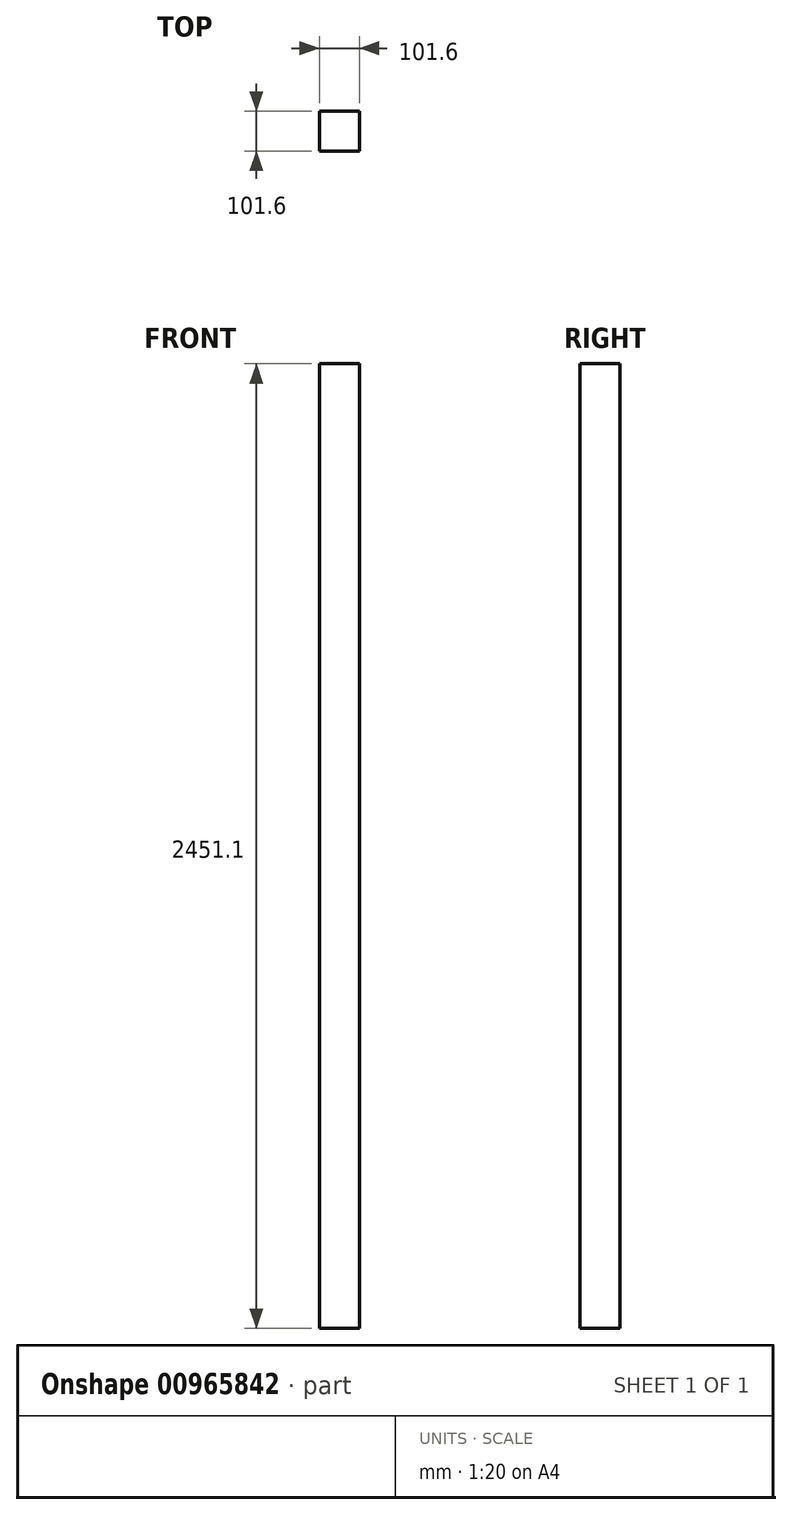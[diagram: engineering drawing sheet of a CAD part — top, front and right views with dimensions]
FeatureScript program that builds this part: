
annotation { "Feature Type Name" : "Feature", "Feature Type Description" : "" }
export const myFeature = defineFeature(function(context is Context, id is Id, definition is map)
    precondition{}
    {
        {
            var Q0;
            Q0=qCreatedBy(makeId("Top.planeOp"),FACE);
            var sketch = newSketch(context, id + "F0", { "sketchPlane" : qUnion([Q0])});
            skPoint(sketch, "E0.top.end.orphan", {"position": v(0, -186.56) * mm});
            skLineSegment(sketch, "E1", {"start": v(102.43, -32.28) * mm, "end": v(204.03, -32.28) * mm});
            skLineSegment(sketch, "E2", {"start": v(204.03, -32.28) * mm, "end": v(204.03, -133.88) * mm});
            skLineSegment(sketch, "E3", {"start": v(204.03, -133.88) * mm, "end": v(102.43, -133.88) * mm});
            skLineSegment(sketch, "E4", {"start": v(102.43, -133.88) * mm, "end": v(102.43, -32.28) * mm});
            skSolve(sketch);
        }
        {
            var Q0;
            Q0=makeQuery(id+"F0.imprint","IMPRINT",FACE,{"disambiguationData":[TD([[makeQuery(id+"F0.imprint","IMPRINT",EDGE,{"derivedFrom":sQuery(id+"F0.wireOp",EDGE,"E1")}),-1.0]])]});
            extrude(context, id + "F1", {"entities" : qUnion([Q0]), "depth" : 2451.1 * mm, "offsetDistance" : 25.4 * mm});
        }
    });
